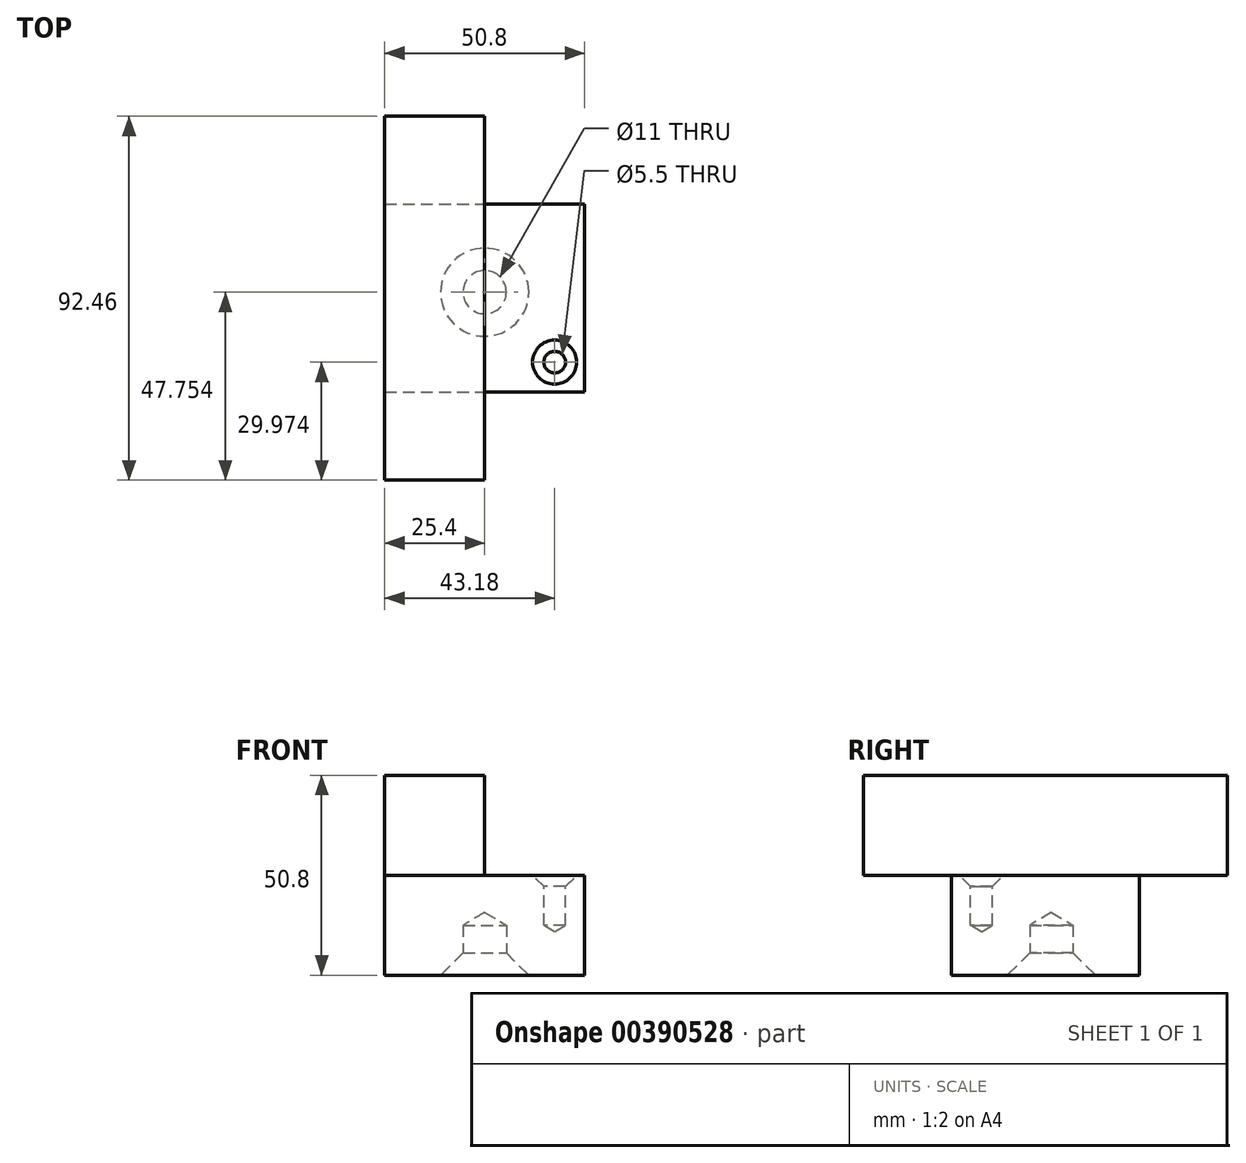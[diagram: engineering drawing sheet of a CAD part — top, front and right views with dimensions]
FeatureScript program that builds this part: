
annotation { "Feature Type Name" : "Feature", "Feature Type Description" : "" }
export const myFeature = defineFeature(function(context is Context, id is Id, definition is map)
    precondition{}
    {
        {
            var Q0;
            Q0=qCreatedBy(makeId("Front.planeOp"),FACE);
            var sketch = newSketch(context, id + "F0", { "sketchPlane" : qUnion([Q0])});
            skLineSegment(sketch, "E0.bottom", {"start": v(-25.4, -12.7) * mm, "end": v(25.4, -12.7) * mm});
            skLineSegment(sketch, "E0.top", {"start": v(-25.4, 12.7) * mm, "end": v(25.4, 12.7) * mm});
            skLineSegment(sketch, "E0.left", {"start": v(-25.4, -12.7) * mm, "end": v(-25.4, 12.7) * mm});
            skLineSegment(sketch, "E0.right", {"start": v(25.4, -12.7) * mm, "end": v(25.4, 12.7) * mm});
            skPoint(sketch, "E0.middle", {"position": v(0, 0) * mm});
            skLineSegment(sketch, "E1", {"start": v(-25.4, 12.7) * mm, "end": v(-25.4, 38.1) * mm});
            skLineSegment(sketch, "E2", {"start": v(-25.4, 38.1) * mm, "end": v(0, 38.1) * mm});
            skLineSegment(sketch, "E3", {"start": v(0, 38.1) * mm, "end": v(0, 12.7) * mm});
            skSolve(sketch);
        }
        {
            var Q0;
            {var subQ0=sQuery(id+"F0.wireOp",EDGE,"E1");Q0=makeQuery(id+"F0.imprint","IMPRINT",FACE,{"disambiguationData":[TD([[makeQuery(id+"F0.imprint","IMPRINT",EDGE,{"derivedFrom":subQ0}),-1.0]])]});}
            var sketch = newSketch(context, id + "F1", { "sketchPlane" : qUnion([Q0])});
            skSolve(sketch);
        }
        {
            var Q0;
            Q0=makeQuery(id+"F0.imprint","IMPRINT",FACE,{"disambiguationData":[TD([[makeQuery(id+"F0.imprint","IMPRINT",EDGE,{"derivedFrom":sQuery(id+"F0.wireOp",EDGE,"E0.bottom")}),1.0]])]});
            var sketch = newSketch(context, id + "F2", { "sketchPlane" : qUnion([Q0])});
            skSolve(sketch);
        }
        {
            var Q0;
            Q0 = qSketchRegion(id + "F1", true);
            var Q1;
            {var subQ0=sQuery(id+"F0.wireOp",EDGE,"E1");Q1=makeQuery(id+"F1.imprint","IMPRINT",FACE,{"disambiguationData":[TD([[makeQuery(id+"F1.imprint","IMPRINT",EDGE,{"derivedFrom":makeQuery(id+"F0.imprint","IMPRINT",EDGE,{"derivedFrom":subQ0})}),-1.0]])]});}
            extrude(context, id + "F3", {"entities" : qUnion([Q0, Q1]), "endBound" : BoundingType.SYMMETRIC, "depth" : 92.46 * mm});
        }
        {
            var Q0;
            Q0=makeQuery(id+"F2.imprint","IMPRINT",FACE,{"disambiguationData":[TD([[makeQuery(id+"F2.imprint","IMPRINT",EDGE,{"derivedFrom":makeQuery(id+"F0.imprint","IMPRINT",EDGE,{"derivedFrom":sQuery(id+"F0.wireOp",EDGE,"E0.bottom")})}),1.0]])]});
            extrude(context, id + "F4", {"entities" : qUnion([Q0]), "operationType" : NewBodyOperationType.ADD, "endBound" : BoundingType.SYMMETRIC, "depth" : 47.75 * mm});
        }
        {
            var Q0;
            Q0=makeQuery(id+"F4.opExtrude","SWEPT_FACE",FACE,{"disambiguationData":[OSD([sQuery(id+"F0.wireOp",EDGE,"E0.bottom")])]});
            var sketch = newSketch(context, id + "F5", { "sketchPlane" : qUnion([Q0])});
            skCircle(sketch, "E4", {"center": v(0, -1.52) * mm, "radius": 3.45 * mm});
            skSolve(sketch);
        }
        {
            var Q0;
            Q0=sQuery(id+"F5.wireOp",VERTEX,"E4.center");
            var Q1;
            Q1=makeQuery(id+"F3.opExtrude","SWEPT_BODY",BODY,{"disambiguationData":[OSD([sQuery(id+"F0.wireOp",EDGE,"E0.top"),sQuery(id+"F0.wireOp",EDGE,"E1"),sQuery(id+"F0.wireOp",EDGE,"E2"),sQuery(id+"F0.wireOp",EDGE,"E3")])]});
            hole(context, id + "F6", {"style" : HoleStyle.C_SINK, "endStyle" : HoleEndStyle.BLIND, "standardTappedOrClearance" : lookupTablePath({ "standard" : "ISO", "fit" : "Normal", "size" : "M10", "type" : "Clearance" }), "standardBlindInLast" : lookupTablePath({ "fit" : "Standard", "standard" : "ISO", "size" : "M10", "type" : "Clearance" }), "holeDiameter" : 11 * mm, "cSinkDiameter" : 22.4 * mm, "cSinkAngle" : 90 * degree, "holeDepth" : 12.7 * mm, "isTappedThrough" : true, "tappedDepth" : 12.7 * mm, "tapClearance" : 3, "startFromSketch" : true, "locations" : qUnion([Q0]), "scope" : qUnion([Q1])});
        }
        {
            var Q0;
            Q0=makeQuery(id+"F4.opExtrude","SWEPT_FACE",FACE,{"disambiguationData":[OSD([sQuery(id+"F0.wireOp",EDGE,"E0.top")])]});
            var sketch = newSketch(context, id + "F7", { "sketchPlane" : qUnion([Q0])});
            skPoint(sketch, "E5", {"position": v(17.78, -16.26) * mm});
            skSolve(sketch);
        }
        {
            var Q0;
            Q0=sQuery(id+"F7.wireOp",VERTEX,"E5");
            var Q1;
            Q1=makeQuery(id+"F3.opExtrude","SWEPT_BODY",BODY,{"disambiguationData":[OSD([sQuery(id+"F0.wireOp",EDGE,"E0.top"),sQuery(id+"F0.wireOp",EDGE,"E1"),sQuery(id+"F0.wireOp",EDGE,"E2"),sQuery(id+"F0.wireOp",EDGE,"E3")])]});
            hole(context, id + "F8", {"style" : HoleStyle.C_SINK, "endStyle" : HoleEndStyle.BLIND, "standardTappedOrClearance" : lookupTablePath({ "standard" : "ISO", "fit" : "Normal", "size" : "M5", "type" : "Clearance" }), "standardBlindInLast" : lookupTablePath({ "fit" : "Standard", "standard" : "ISO", "size" : "M5", "type" : "Clearance" }), "holeDiameter" : 5.5 * mm, "cSinkDiameter" : 11.2 * mm, "cSinkAngle" : 90 * degree, "holeDepth" : 12.7 * mm, "isTappedThrough" : true, "tappedDepth" : 12.7 * mm, "tapClearance" : 3, "startFromSketch" : true, "locations" : qUnion([Q0]), "scope" : qUnion([Q1])});
        }
    });
